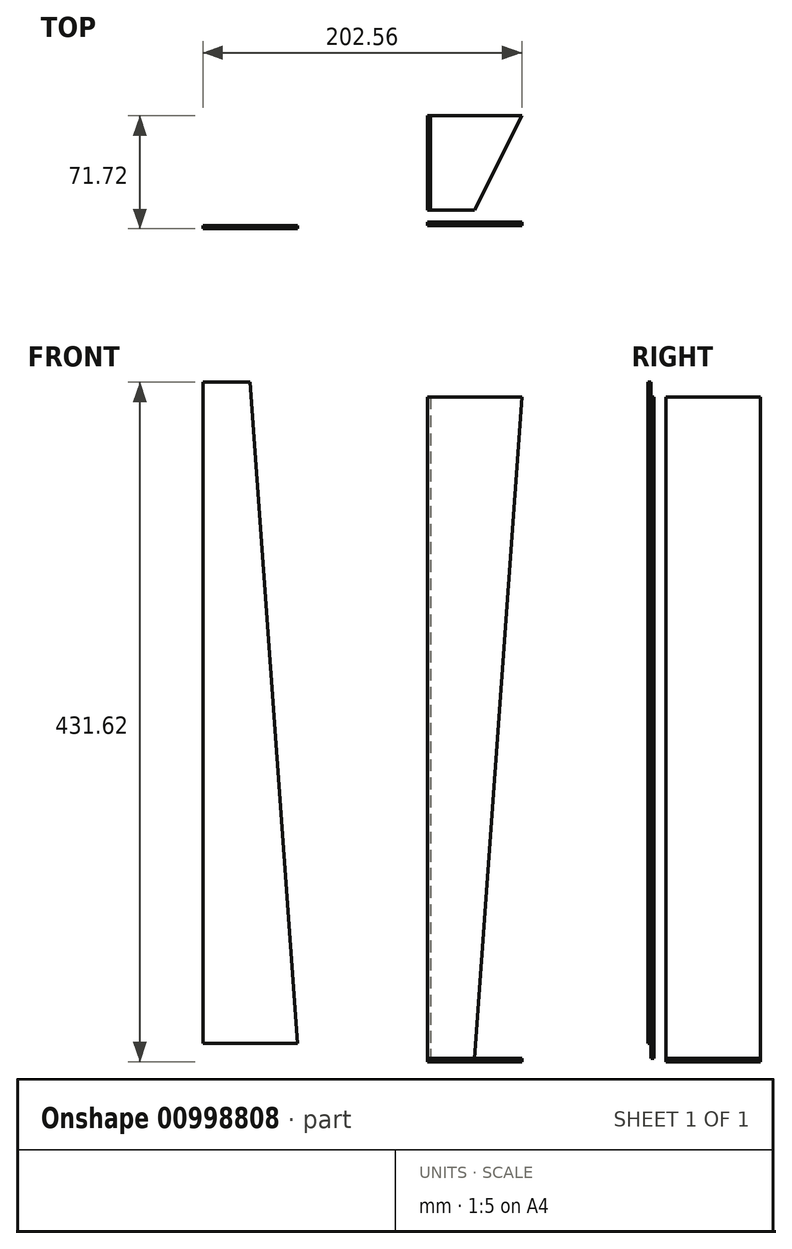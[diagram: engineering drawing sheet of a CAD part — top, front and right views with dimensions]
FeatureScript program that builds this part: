
annotation { "Feature Type Name" : "Feature", "Feature Type Description" : "" }
export const myFeature = defineFeature(function(context is Context, id is Id, definition is map)
    precondition{}
    {
        {
            var Q0;
            Q0=qCreatedBy(makeId("Top.planeOp"),FACE);
            var sketch = newSketch(context, id + "F0", { "sketchPlane" : qUnion([Q0])});
            skLineSegment(sketch, "E0", {"start": v(153.67, 69.72) * mm, "end": v(213.67, 69.72) * mm});
            skLineSegment(sketch, "E1", {"start": v(153.67, 69.72) * mm, "end": v(153.67, 9.72) * mm});
            skLineSegment(sketch, "E2", {"start": v(153.67, 9.72) * mm, "end": v(183.67, 9.72) * mm});
            skLineSegment(sketch, "E3", {"start": v(183.67, 9.72) * mm, "end": v(213.67, 69.72) * mm});
            skSolve(sketch);
        }
        {
            var Q0;
            Q0=makeQuery(id+"F0.imprint","IMPRINT",FACE,{"disambiguationData":[TD([[makeQuery(id+"F0.imprint","IMPRINT",EDGE,{"derivedFrom":sQuery(id+"F0.wireOp",EDGE,"E0")}),-1.0]])]});
            extrude(context, id + "F1", {"entities" : qUnion([Q0]), "depth" : 2 * mm, "offsetDistance" : 25 * mm});
        }
        {
            var Q0;
            Q0=qCreatedBy(makeId("Front.planeOp"),FACE);
            var sketch = newSketch(context, id + "F2", { "sketchPlane" : qUnion([Q0])});
            skLineSegment(sketch, "E4", {"start": v(183.67, 2) * mm, "end": v(153.67, 2) * mm});
            skLineSegment(sketch, "E5", {"start": v(153.67, 2) * mm, "end": v(153.67, 422) * mm});
            skLineSegment(sketch, "E6", {"start": v(153.67, 422) * mm, "end": v(213.67, 422) * mm});
            skLineSegment(sketch, "E7", {"start": v(213.67, 422) * mm, "end": v(183.67, 2) * mm});
            skSolve(sketch);
        }
        {
            var Q0;
            Q0=makeQuery(id+"F2.imprint","IMPRINT",FACE,{"disambiguationData":[TD([[makeQuery(id+"F2.imprint","IMPRINT",EDGE,{"derivedFrom":sQuery(id+"F2.wireOp",EDGE,"E4")}),-1.0]])]});
            extrude(context, id + "F3", {"entities" : qUnion([Q0]), "oppositeDirection" : true, "depth" : 2 * mm, "offsetDistance" : 25 * mm});
        }
        {
            var Q0;
            Q0=qCreatedBy(makeId("Front.planeOp"),FACE);
            var sketch = newSketch(context, id + "F4", { "sketchPlane" : qUnion([Q0])});
            skLineSegment(sketch, "E8", {"start": v(71.1, 11.62) * mm, "end": v(11.1, 11.62) * mm});
            skLineSegment(sketch, "E9", {"start": v(11.1, 11.62) * mm, "end": v(11.1, 431.62) * mm});
            skLineSegment(sketch, "E10", {"start": v(11.1, 431.62) * mm, "end": v(41.1, 431.62) * mm});
            skLineSegment(sketch, "E11", {"start": v(41.1, 431.62) * mm, "end": v(71.1, 11.62) * mm});
            skSolve(sketch);
        }
        {
            var Q0;
            Q0=makeQuery(id+"F4.imprint","IMPRINT",FACE,{"disambiguationData":[TD([[makeQuery(id+"F4.imprint","IMPRINT",EDGE,{"derivedFrom":sQuery(id+"F4.wireOp",EDGE,"E8")}),-1.0]])]});
            extrude(context, id + "F5", {"entities" : qUnion([Q0]), "depth" : 2 * mm, "offsetDistance" : 25 * mm});
        }
        {
            var Q0;
            Q0=makeQuery(id+"F1.opExtrude","CAP_FACE",FACE,{"disambiguationData":[OSD([sQuery(id+"F0.wireOp",EDGE,"E0"),sQuery(id+"F0.wireOp",EDGE,"E1"),sQuery(id+"F0.wireOp",EDGE,"E2"),sQuery(id+"F0.wireOp",EDGE,"E3")])],"isStart":false});
            var sketch = newSketch(context, id + "F6", { "sketchPlane" : qUnion([Q0])});
            skLineSegment(sketch, "E12", {"start": v(155.67, 69.72) * mm, "end": v(155.67, 9.72) * mm});
            skSolve(sketch);
        }
        {
            var Q0;
            {var subQ0=sQuery(id+"F6.wireOp",EDGE,"E12");Q0=makeQuery(id+"F6.imprint","IMPRINT",FACE,{"disambiguationData":[TD([[makeQuery(id+"F6.imprint","IMPRINT",EDGE,{"derivedFrom":subQ0}),-1.0]])]});}
            extrude(context, id + "F7", {"entities" : qUnion([Q0]), "operationType" : NewBodyOperationType.ADD, "depth" : 420 * mm, "offsetDistance" : 25 * mm});
        }
    });
